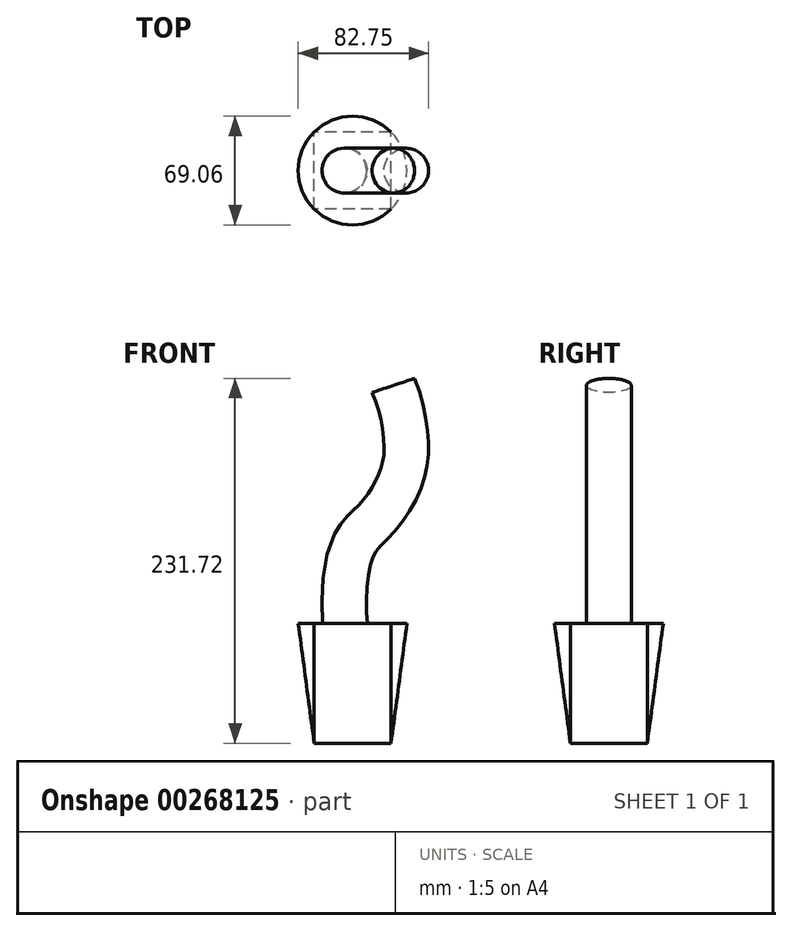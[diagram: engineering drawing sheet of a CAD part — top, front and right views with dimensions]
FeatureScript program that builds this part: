
annotation { "Feature Type Name" : "Feature", "Feature Type Description" : "" }
export const myFeature = defineFeature(function(context is Context, id is Id, definition is map)
    precondition{}
    {
        {
            var Q0;
            Q0=qCreatedBy(makeId("Top.planeOp"),FACE);
            var sketch = newSketch(context, id + "F0", { "sketchPlane" : qUnion([Q0])});
            skCircle(sketch, "E0", {"center": v(0, 0) * mm, "radius": 34.53 * mm});
            skSolve(sketch);
        }
        {
            var Q0;
            Q0=qCreatedBy(makeId("Top.planeOp"),FACE);
            cPlane(context, id + "F1", {"entities" : qUnion([Q0]), "cplaneType" : CPlaneType.OFFSET, "offset" : 76.2 * mm, "oppositeDirection" : true, "width" : 152.4 * mm, "height" : 152.4 * mm});
        }
        {
            var Q0;
            Q0=qCreatedBy(id+"F1.planeOp",FACE);
            var sketch = newSketch(context, id + "F2", { "sketchPlane" : qUnion([Q0])});
            skLineSegment(sketch, "E1.bottom", {"start": v(24.42, -24.42) * mm, "end": v(-24.42, -24.42) * mm});
            skLineSegment(sketch, "E1.top", {"start": v(24.42, 24.42) * mm, "end": v(-24.42, 24.42) * mm});
            skLineSegment(sketch, "E1.left", {"start": v(24.42, -24.42) * mm, "end": v(24.42, 24.42) * mm});
            skLineSegment(sketch, "E1.right", {"start": v(-24.42, -24.42) * mm, "end": v(-24.42, 24.42) * mm});
            skPoint(sketch, "E1.middle", {"position": v(0, 0) * mm});
            skSolve(sketch);
        }
        {
            var Q0;
            Q0=makeQuery(id+"F2.imprint","IMPRINT",FACE,{"disambiguationData":[TD([[makeQuery(id+"F2.imprint","IMPRINT",EDGE,{"derivedFrom":sQuery(id+"F2.wireOp",EDGE,"E1.bottom")}),-1.0]])]});
            var Q1;
            Q1=makeQuery(id+"F0.imprint","IMPRINT",FACE,{"disambiguationData":[TD([[makeQuery(id+"F0.imprint","IMPRINT",EDGE,{"derivedFrom":sQuery(id+"F0.wireOp",EDGE,"E0")}),1.0]])]});
            loft(context, id + "F3", {"sheetProfilesArray" : [{ "sheetProfileEntities" : qUnion([Q0]) }, { "sheetProfileEntities" : qUnion([Q1]) }]});
        }
        {
            var Q0;
            Q0=qCreatedBy(makeId("Top.planeOp"),FACE);
            var sketch = newSketch(context, id + "F4", { "sketchPlane" : qUnion([Q0])});
            skCircle(sketch, "E2", {"center": v(-83.75, 0) * mm, "radius": 14.2 * mm});
            skSolve(sketch);
        }
        {
            var Q0;
            Q0=qCreatedBy(makeId("Front.planeOp"),FACE);
            var sketch = newSketch(context, id + "F5", { "sketchPlane" : qUnion([Q0])});
            skFitSpline(sketch, "E3", {"points": [v(-83.75, 0) * mm, v(-79.05, 47.46) * mm, v(-62.93, 67.6) * mm, v(-47.97, 92.94) * mm, v(-45.1, 116.54) * mm, v(-53.15, 151.07) * mm], "startDerivative": vector(-17.16, 162.09) * mm, "endDerivative": vector(-68.54, 151.88) * mm});
            skSolve(sketch);
        }
        {
            var Q0;
            Q0=makeQuery(id+"F4.imprint","IMPRINT",FACE,{"disambiguationData":[TD([[makeQuery(id+"F4.imprint","IMPRINT",EDGE,{"derivedFrom":sQuery(id+"F4.wireOp",EDGE,"E2")}),1.0]])]});
            var Q1;
            Q1=sQuery(id+"F5.wireOp",EDGE,"E3");
            sweep(context, id + "F6", {"profiles" : qUnion([Q0]), "path" : qUnion([Q1])});
        }
        {
            var Q0;
            Q0=makeQuery(id+"F6.opSweep","SWEPT_BODY",BODY,{"disambiguationData":[OSD([sQuery(id+"F4.wireOp",EDGE,"E2"),sQuery(id+"F5.wireOp",EDGE,"E3")])]});
            var Q1;
            Q1=qCreatedBy(makeId("Origin.pointOp"),VERTEX);
            transform(context, id + "F7", {"entities" : qUnion([Q0]), "transformType" : TransformType.TRANSLATION_3D, "dx" : 79 * mm, "dy" : 0 * mm, "dz" : 0 * mm, "makeCopy" : false});
        }
    });
